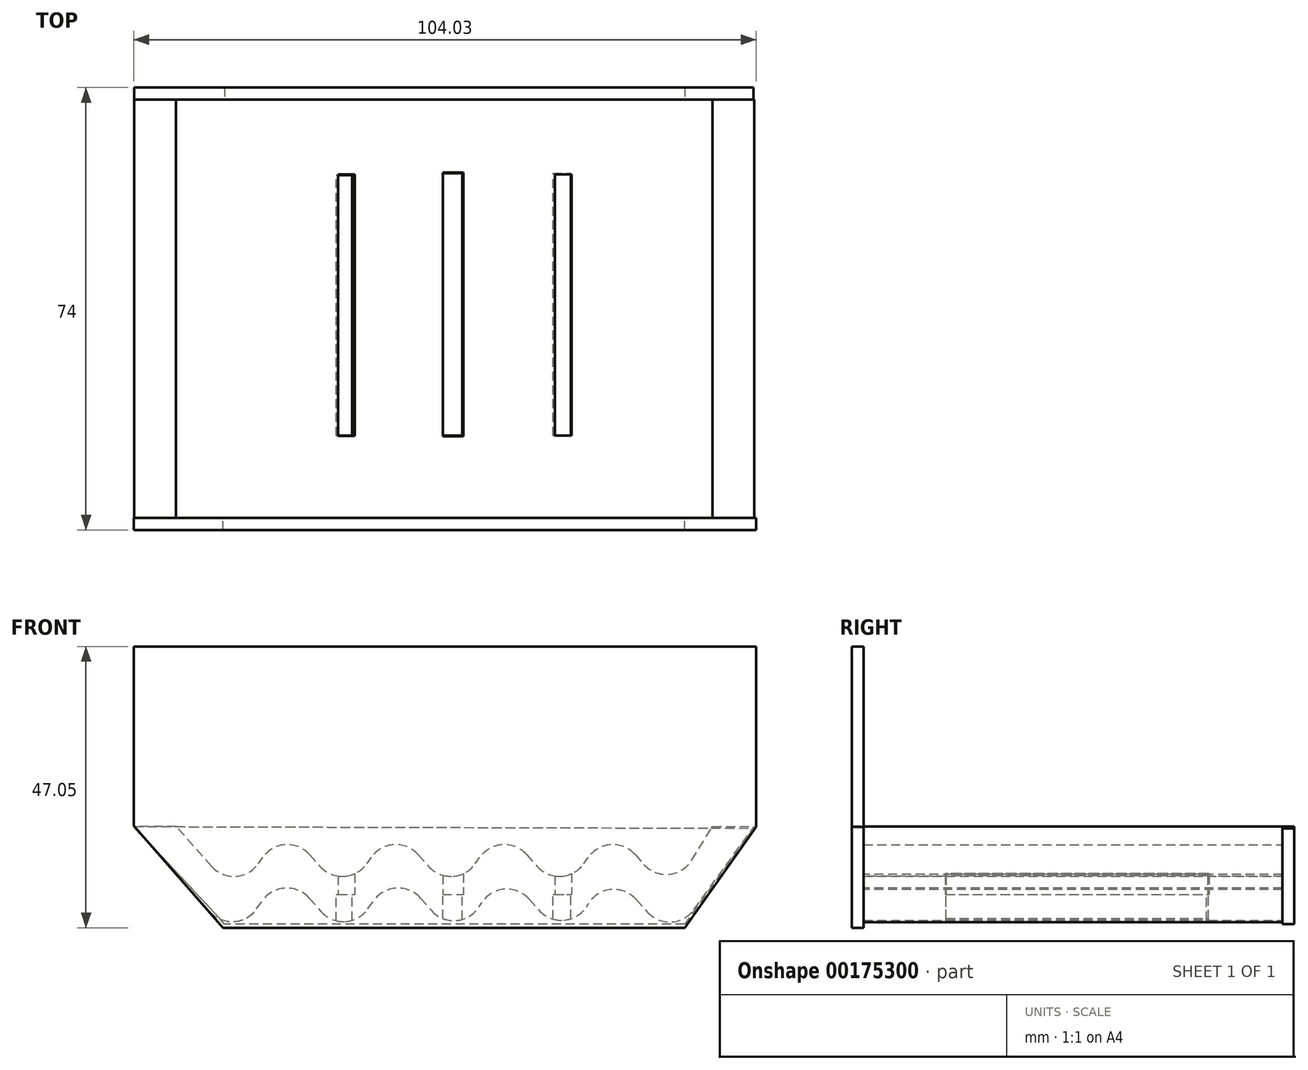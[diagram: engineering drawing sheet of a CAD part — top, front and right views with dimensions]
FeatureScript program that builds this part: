
annotation { "Feature Type Name" : "Feature", "Feature Type Description" : "" }
export const myFeature = defineFeature(function(context is Context, id is Id, definition is map)
    precondition{}
    {
        {
            var Q0;
            Q0=qCreatedBy(makeId("Front.planeOp"),FACE);
            var sketch = newSketch(context, id + "F0", { "sketchPlane" : qUnion([Q0])});
            skLineSegment(sketch, "E0", {"start": v(-54.44, 0) * mm, "end": v(-46.4, 11.4) * mm});
            skLineSegment(sketch, "E1", {"start": v(-46.4, 11.4) * mm, "end": v(-36.3, 0) * mm});
            skLineSegment(sketch, "E2", {"start": v(-36.3, 0) * mm, "end": v(-28.26, 11.4) * mm});
            skLineSegment(sketch, "E3", {"start": v(-28.26, 11.4) * mm, "end": v(-18.15, 0) * mm});
            skLineSegment(sketch, "E4", {"start": v(-18.15, 0) * mm, "end": v(-10.11, 11.4) * mm});
            skLineSegment(sketch, "E5", {"start": v(-10.11, 11.4) * mm, "end": v(0, 0) * mm});
            skLineSegment(sketch, "E6", {"start": v(0, 0) * mm, "end": v(8.04, 11.4) * mm});
            skLineSegment(sketch, "E7", {"start": v(8.04, 11.4) * mm, "end": v(18.15, 0) * mm});
            skLineSegment(sketch, "E8", {"start": v(-54.44, 0) * mm, "end": v(-64.56, 11.4) * mm});
            skLineSegment(sketch, "E9", {"start": v(-64.56, 11.4) * mm, "end": v(-71.56, 11.4) * mm});
            skLineSegment(sketch, "E10", {"start": v(-71.56, 11.4) * mm, "end": v(-54.73, -7.57) * mm});
            skLineSegment(sketch, "E11", {"start": v(18.15, 0) * mm, "end": v(25.15, 11.4) * mm});
            skLineSegment(sketch, "E12", {"start": v(25.15, 11.4) * mm, "end": v(32.15, 11.4) * mm});
            skLineSegment(sketch, "E13", {"start": v(-54.73, -7.57) * mm, "end": v(-46.49, 4.12) * mm});
            skLineSegment(sketch, "E14", {"start": v(-46.49, 4.12) * mm, "end": v(-36.12, -7.57) * mm});
            skLineSegment(sketch, "E15", {"start": v(-36.12, -7.57) * mm, "end": v(-27.88, 4.12) * mm});
            skLineSegment(sketch, "E16", {"start": v(-27.88, 4.12) * mm, "end": v(-17.5, -7.57) * mm});
            skLineSegment(sketch, "E17", {"start": v(-17.5, -7.57) * mm, "end": v(-9.83, 4.12) * mm});
            skLineSegment(sketch, "E18", {"start": v(-9.83, 4.12) * mm, "end": v(0.53, -7.57) * mm});
            skLineSegment(sketch, "E19", {"start": v(0.53, -7.57) * mm, "end": v(8.01, 4.12) * mm});
            skLineSegment(sketch, "E20", {"start": v(8.01, 4.12) * mm, "end": v(18.38, -7.57) * mm});
            skLineSegment(sketch, "E21", {"start": v(18.38, -7.57) * mm, "end": v(32.15, 11.4) * mm});
            skSolve(sketch);
        }
        {
            var Q0;
            Q0 = qSketchRegion(id + "F0", true);
            extrude(context, id + "F1", {"entities" : qUnion([Q0]), "depth" : 70 * mm});
        }
        {
            var Q0;
            Q0=makeQuery(id+"F1.opExtrude","SWEPT_EDGE",EDGE,{"disambiguationData":[OSD([sQuery(id+"F0.wireOp",EDGE,"E10"),sQuery(id+"F0.wireOp",EDGE,"E13")])]});
            var Q1;
            Q1=makeQuery(id+"F1.opExtrude","SWEPT_EDGE",EDGE,{"disambiguationData":[OSD([sQuery(id+"F0.wireOp",EDGE,"E14"),sQuery(id+"F0.wireOp",EDGE,"E15")])]});
            var Q2;
            Q2=makeQuery(id+"F1.opExtrude","SWEPT_EDGE",EDGE,{"disambiguationData":[OSD([sQuery(id+"F0.wireOp",EDGE,"E16"),sQuery(id+"F0.wireOp",EDGE,"E17")])]});
            var Q3;
            Q3=makeQuery(id+"F1.opExtrude","SWEPT_EDGE",EDGE,{"disambiguationData":[OSD([sQuery(id+"F0.wireOp",EDGE,"E18"),sQuery(id+"F0.wireOp",EDGE,"E19")])]});
            var Q4;
            Q4=makeQuery(id+"F1.opExtrude","SWEPT_EDGE",EDGE,{"disambiguationData":[OSD([sQuery(id+"F0.wireOp",EDGE,"E20"),sQuery(id+"F0.wireOp",EDGE,"E21")])]});
            var Q5;
            Q5=makeQuery(id+"F1.opExtrude","SWEPT_EDGE",EDGE,{"disambiguationData":[OSD([sQuery(id+"F0.wireOp",EDGE,"E0"),sQuery(id+"F0.wireOp",EDGE,"E8")])]});
            var Q6;
            Q6=makeQuery(id+"F1.opExtrude","SWEPT_EDGE",EDGE,{"disambiguationData":[OSD([sQuery(id+"F0.wireOp",EDGE,"E1"),sQuery(id+"F0.wireOp",EDGE,"E2")])]});
            var Q7;
            Q7=makeQuery(id+"F1.opExtrude","SWEPT_EDGE",EDGE,{"disambiguationData":[OSD([sQuery(id+"F0.wireOp",EDGE,"E3"),sQuery(id+"F0.wireOp",EDGE,"E4")])]});
            var Q8;
            Q8=makeQuery(id+"F1.opExtrude","SWEPT_EDGE",EDGE,{"disambiguationData":[OSD([sQuery(id+"F0.wireOp",EDGE,"E7"),sQuery(id+"F0.wireOp",EDGE,"E11")])]});
            var Q9;
            Q9=makeQuery(id+"F1.opExtrude","SWEPT_EDGE",EDGE,{"disambiguationData":[OSD([sQuery(id+"F0.wireOp",EDGE,"E5"),sQuery(id+"F0.wireOp",EDGE,"E6")])]});
            var Q10;
            Q10=makeQuery(id+"F1.opExtrude","SWEPT_EDGE",EDGE,{"disambiguationData":[OSD([sQuery(id+"F0.wireOp",EDGE,"E0"),sQuery(id+"F0.wireOp",EDGE,"E1")])]});
            var Q11;
            Q11=makeQuery(id+"F1.opExtrude","SWEPT_EDGE",EDGE,{"disambiguationData":[OSD([sQuery(id+"F0.wireOp",EDGE,"E2"),sQuery(id+"F0.wireOp",EDGE,"E3")])]});
            var Q12;
            Q12=makeQuery(id+"F1.opExtrude","SWEPT_EDGE",EDGE,{"disambiguationData":[OSD([sQuery(id+"F0.wireOp",EDGE,"E4"),sQuery(id+"F0.wireOp",EDGE,"E5")])]});
            var Q13;
            Q13=makeQuery(id+"F1.opExtrude","SWEPT_EDGE",EDGE,{"disambiguationData":[OSD([sQuery(id+"F0.wireOp",EDGE,"E6"),sQuery(id+"F0.wireOp",EDGE,"E7")])]});
            var Q14;
            Q14=makeQuery(id+"F1.opExtrude","SWEPT_EDGE",EDGE,{"disambiguationData":[OSD([sQuery(id+"F0.wireOp",EDGE,"E13"),sQuery(id+"F0.wireOp",EDGE,"E14")])]});
            var Q15;
            Q15=makeQuery(id+"F1.opExtrude","SWEPT_EDGE",EDGE,{"disambiguationData":[OSD([sQuery(id+"F0.wireOp",EDGE,"E15"),sQuery(id+"F0.wireOp",EDGE,"E16")])]});
            var Q16;
            Q16=makeQuery(id+"F1.opExtrude","SWEPT_EDGE",EDGE,{"disambiguationData":[OSD([sQuery(id+"F0.wireOp",EDGE,"E17"),sQuery(id+"F0.wireOp",EDGE,"E18")])]});
            var Q17;
            Q17=makeQuery(id+"F1.opExtrude","SWEPT_EDGE",EDGE,{"disambiguationData":[OSD([sQuery(id+"F0.wireOp",EDGE,"E19"),sQuery(id+"F0.wireOp",EDGE,"E20")])]});
            fillet(context, id + "F2", {"entities" : qUnion([Q0, Q1, Q2, Q3, Q4, Q5, Q6, Q7, Q8, Q9, Q10, Q11, Q12, Q13, Q14, Q15, Q16, Q17]), "radius" : 5 * mm, "tangentPropagation" : true, "allowEdgeOverflow" : false});
        }
        {
            var Q0;
            Q0=qCreatedBy(makeId("Front.planeOp"),FACE);
            var sketch = newSketch(context, id + "F3", { "sketchPlane" : qUnion([Q0])});
            skLineSegment(sketch, "E22", {"start": v(32, 11.09) * mm, "end": v(20.5, -4.91) * mm});
            skLineSegment(sketch, "E23", {"start": v(20.5, -4.91) * mm, "end": v(-56.43, -4.91) * mm});
            skLineSegment(sketch, "E24", {"start": v(-56.43, -4.91) * mm, "end": v(-71.6, 11.37) * mm});
            skLineSegment(sketch, "E25", {"start": v(-71.6, 11.37) * mm, "end": v(32, 11.09) * mm});
            skSolve(sketch);
        }
        {
            var Q0;
            Q0 = qSketchRegion(id + "F3", true);
            extrude(context, id + "F4", {"entities" : qUnion([Q0]), "operationType" : NewBodyOperationType.ADD, "oppositeDirection" : true, "depth" : 2 * mm});
        }
        {
            var Q0;
            Q0=makeQuery(id+"F1.opExtrude","CAP_FACE",FACE,{"disambiguationData":[OSD([sQuery(id+"F0.wireOp",EDGE,"E0"),sQuery(id+"F0.wireOp",EDGE,"E1"),sQuery(id+"F0.wireOp",EDGE,"E2"),sQuery(id+"F0.wireOp",EDGE,"E3"),sQuery(id+"F0.wireOp",EDGE,"E4"),sQuery(id+"F0.wireOp",EDGE,"E5"),sQuery(id+"F0.wireOp",EDGE,"E6"),sQuery(id+"F0.wireOp",EDGE,"E7"),sQuery(id+"F0.wireOp",EDGE,"E8"),sQuery(id+"F0.wireOp",EDGE,"E9"),sQuery(id+"F0.wireOp",EDGE,"E10"),sQuery(id+"F0.wireOp",EDGE,"E11"),sQuery(id+"F0.wireOp",EDGE,"E12"),sQuery(id+"F0.wireOp",EDGE,"E13"),sQuery(id+"F0.wireOp",EDGE,"E14"),sQuery(id+"F0.wireOp",EDGE,"E15"),sQuery(id+"F0.wireOp",EDGE,"E16"),sQuery(id+"F0.wireOp",EDGE,"E17"),sQuery(id+"F0.wireOp",EDGE,"E18"),sQuery(id+"F0.wireOp",EDGE,"E19"),sQuery(id+"F0.wireOp",EDGE,"E20"),sQuery(id+"F0.wireOp",EDGE,"E21")])],"isStart":false});
            var sketch = newSketch(context, id + "F5", { "sketchPlane" : qUnion([Q0])});
            skLineSegment(sketch, "E26", {"start": v(-71.56, 11.4) * mm, "end": v(32.15, 11.4) * mm});
            skLineSegment(sketch, "E27", {"start": v(32.15, 11.4) * mm, "end": v(20.3, -4.94) * mm});
            skLineSegment(sketch, "E28", {"start": v(20.3, -4.94) * mm, "end": v(-55.46, -4.52) * mm});
            skPoint(sketch, "E28.endSnap0", {"position": v(-54.9, -4.52) * mm});
            skLineSegment(sketch, "E29", {"start": v(-71.56, 11.4) * mm, "end": v(-55.46, -4.52) * mm});
            skSolve(sketch);
        }
        {
            var Q0;
            {var subQ22=sQuery(id+"F5.wireOp",EDGE,"E29");Q0=makeQuery(id+"F5.imprint","IMPRINT",FACE,{"disambiguationData":[TD([[makeQuery(id+"F5.imprint","IMPRINT",EDGE,{"derivedFrom":subQ22}),1.0]])]});}
            var sketch = newSketch(context, id + "F6", { "sketchPlane" : qUnion([Q0])});
            skLineSegment(sketch, "E30", {"start": v(-71.6, 11.52) * mm, "end": v(-56.7, -5.55) * mm});
            skLineSegment(sketch, "E31", {"start": v(-56.7, -5.55) * mm, "end": v(20.52, -5.55) * mm});
            skLineSegment(sketch, "E32", {"start": v(20.52, -5.55) * mm, "end": v(32.43, 11.32) * mm});
            skLineSegment(sketch, "E33", {"start": v(32.43, 11.32) * mm, "end": v(32.43, 41.5) * mm});
            skLineSegment(sketch, "E34", {"start": v(32.43, 41.5) * mm, "end": v(-71.6, 41.5) * mm});
            skLineSegment(sketch, "E35", {"start": v(-71.6, 11.52) * mm, "end": v(-71.6, 41.5) * mm});
            skSolve(sketch);
        }
        {
            var Q0;
            Q0 = qSketchRegion(id + "F6", true);
            extrude(context, id + "F7", {"entities" : qUnion([Q0]), "operationType" : NewBodyOperationType.ADD, "depth" : 2 * mm});
        }
        {
            var Q0;
            Q0=qCreatedBy(makeId("Top.planeOp"),FACE);
            var sketch = newSketch(context, id + "F8", { "sketchPlane" : qUnion([Q0])});
            skLineSegment(sketch, "E36", {"start": v(-37.9, -12.77) * mm, "end": v(-34.81, -12.77) * mm});
            skLineSegment(sketch, "E37", {"start": v(-37.9, -56.3) * mm, "end": v(-34.81, -56.3) * mm});
            skLineSegment(sketch, "E38.left", {"start": v(-37.9, -12.77) * mm, "end": v(-37.9, -56.3) * mm});
            skLineSegment(sketch, "E38.right", {"start": v(-34.81, -12.77) * mm, "end": v(-34.81, -56.3) * mm});
            skLineSegment(sketch, "E39.bottom", {"start": v(-20.21, -12.77) * mm, "end": v(-17.4, -12.77) * mm});
            skLineSegment(sketch, "E39.top", {"start": v(-20.21, -56.3) * mm, "end": v(-17.4, -56.3) * mm});
            skLineSegment(sketch, "E39.left", {"start": v(-20.21, -12.77) * mm, "end": v(-20.21, -56.3) * mm});
            skLineSegment(sketch, "E39.right", {"start": v(-17.4, -12.77) * mm, "end": v(-17.4, -56.3) * mm});
            skLineSegment(sketch, "E40.bottom", {"start": v(1.97, -12.77) * mm, "end": v(-1.82, -12.77) * mm});
            skLineSegment(sketch, "E40.top", {"start": v(1.97, -56.3) * mm, "end": v(-1.82, -56.3) * mm});
            skLineSegment(sketch, "E40.left", {"start": v(1.97, -12.77) * mm, "end": v(1.97, -56.3) * mm});
            skLineSegment(sketch, "E40.right", {"start": v(-1.82, -12.77) * mm, "end": v(-1.82, -56.3) * mm});
            skLineSegment(sketch, "E41.trimOffspring", {"start": v(-1.82, -12.77) * mm, "end": v(1.97, -12.77) * mm});
            skPoint(sketch, "E42.orphan", {"position": v(-75.24, -56.3) * mm});
            skLineSegment(sketch, "E43.trimOffspring", {"start": v(-1.82, -56.3) * mm, "end": v(1.97, -56.3) * mm});
            skPoint(sketch, "E44.orphan", {"position": v(71.6, -56.3) * mm});
            skSolve(sketch);
        }
        {
            var Q0;
            Q0=qCreatedBy(makeId("Top.planeOp"),FACE);
            var sketch = newSketch(context, id + "F9", { "sketchPlane" : qUnion([Q0])});
            skLineSegment(sketch, "E45.bottom", {"start": v(-37.8, -56.23) * mm, "end": v(-35.12, -56.23) * mm});
            skLineSegment(sketch, "E45.top", {"start": v(-37.8, -12.65) * mm, "end": v(-35.12, -12.65) * mm});
            skLineSegment(sketch, "E45.left", {"start": v(-37.8, -56.23) * mm, "end": v(-37.8, -12.65) * mm});
            skLineSegment(sketch, "E45.right", {"start": v(-35.12, -56.23) * mm, "end": v(-35.12, -12.65) * mm});
            skLineSegment(sketch, "E46.bottom", {"start": v(-19.95, -56.23) * mm, "end": v(-16.68, -56.23) * mm});
            skLineSegment(sketch, "E46.top", {"start": v(-19.95, -12.35) * mm, "end": v(-16.68, -12.35) * mm});
            skLineSegment(sketch, "E46.left", {"start": v(-19.95, -56.23) * mm, "end": v(-19.95, -12.35) * mm});
            skLineSegment(sketch, "E46.right", {"start": v(-16.68, -56.23) * mm, "end": v(-16.68, -12.35) * mm});
            skLineSegment(sketch, "E47.bottom", {"start": v(-1.51, -56.23) * mm, "end": v(1.46, -56.23) * mm});
            skLineSegment(sketch, "E47.top", {"start": v(-1.51, -12.35) * mm, "end": v(1.46, -12.35) * mm});
            skLineSegment(sketch, "E47.left", {"start": v(-1.51, -56.23) * mm, "end": v(-1.51, -12.35) * mm});
            skLineSegment(sketch, "E47.right", {"start": v(1.46, -56.23) * mm, "end": v(1.46, -12.35) * mm});
            skSolve(sketch);
        }
        {
            var Q0;
            Q0 = qSketchRegion(id + "F9", true);
            extrude(context, id + "F10", {"entities" : qUnion([Q0]), "operationType" : NewBodyOperationType.REMOVE, "endBound" : BoundingType.THROUGH_ALL, "oppositeDirection" : true, "depth" : 25 * mm});
        }
        {
            var Q0;
            Q0=makeQuery(id+"F8.imprint","IMPRINT",FACE,{"disambiguationData":[TD([[makeQuery(id+"F8.imprint","IMPRINT",EDGE,{"derivedFrom":sQuery(id+"F8.wireOp",EDGE,"E36")}),-1.0]])]});
            var sketch = newSketch(context, id + "F11", { "sketchPlane" : qUnion([Q0])});
            skLineSegment(sketch, "E48.bottom", {"start": v(-37.45, -56.3) * mm, "end": v(-34.67, -56.3) * mm});
            skLineSegment(sketch, "E48.top", {"start": v(-37.45, -12.5) * mm, "end": v(-34.67, -12.5) * mm});
            skLineSegment(sketch, "E48.left", {"start": v(-37.45, -56.3) * mm, "end": v(-37.45, -12.5) * mm});
            skLineSegment(sketch, "E48.right", {"start": v(-34.67, -56.3) * mm, "end": v(-34.67, -12.5) * mm});
            skLineSegment(sketch, "E49.bottom", {"start": v(-19.95, -56.37) * mm, "end": v(-16.53, -56.37) * mm});
            skLineSegment(sketch, "E49.top", {"start": v(-19.95, -12.2) * mm, "end": v(-16.53, -12.2) * mm});
            skLineSegment(sketch, "E49.left", {"start": v(-19.95, -56.37) * mm, "end": v(-19.95, -12.2) * mm});
            skLineSegment(sketch, "E49.right", {"start": v(-16.53, -56.37) * mm, "end": v(-16.53, -12.2) * mm});
            skLineSegment(sketch, "E50.bottom", {"start": v(-1.21, -56.22) * mm, "end": v(1.61, -56.22) * mm});
            skLineSegment(sketch, "E50.top", {"start": v(-1.21, -12.5) * mm, "end": v(1.61, -12.5) * mm});
            skLineSegment(sketch, "E50.left", {"start": v(-1.21, -56.22) * mm, "end": v(-1.21, -12.5) * mm});
            skLineSegment(sketch, "E50.right", {"start": v(1.61, -56.22) * mm, "end": v(1.61, -12.5) * mm});
            skSolve(sketch);
        }
        {
            var Q0;
            Q0 = qSketchRegion(id + "F11", true);
            extrude(context, id + "F12", {"entities" : qUnion([Q0]), "operationType" : NewBodyOperationType.REMOVE, "endBound" : BoundingType.THROUGH_ALL, "depth" : 25 * mm});
        }
    });
